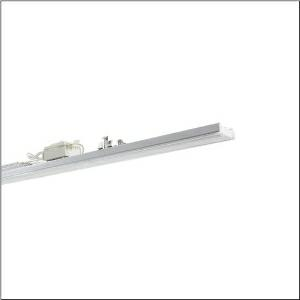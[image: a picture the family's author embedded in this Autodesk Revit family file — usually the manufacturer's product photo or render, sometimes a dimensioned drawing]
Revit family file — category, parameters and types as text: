
# Revit family: licross_11_recessed_mo_51tl18vn455g
name_source: partatom
category: Lighting Fixtures
units: mm (PartAtom-declared; Revit-internal decimal feet)

## family parameters
Cut with Voids When Loaded = No
Host = Face
Light Source = No
Part Type = Normal
Room Calculation Point = No
Round Connector Dimension = Use Diameter
Shared = No

## types (1)
- --- (1 x LED, 5560 lm, 30 W, 4000K)
    Apparent Load = 30 VA
    CIE Flux Codes = 83 96 99 100 100
    Color Rendering = 80
    Color Temperature = 4000K
    Default Elevation = 1800 mm
    Description = Licross 11 Recessed MO, luminaire insert, of sheet steel, galvanised, coil coated, white, length: 1.500mm, width: 66mm, height: 67mm, LED rated luminous flux: 5.560lm, light colour: 840, SDCM (Standard Deviation of Colour Matching)MacAdam ≤ 2 SDCM (initial), control gear: DALI 2, CLO, with plug, 5-pole, with phase selection, mains connection: 220..240V, AC, 50/60Hz, start of lifetime: 30W, end of service life: 34W, internal wiring halogen-free, primary optical cover: cover, of PMMA, light emission: direct distribution, primary light characteristic: symmetric, protection rating (complete): IP40, insulation class (complete): insulation class I (protective earthing), certification: CE, ENEC, VDE, UKCA, protection symbol: D if used in an environment without relevant dust loads with corresponding accessories, impact resistance: IK06, permissible ambient temperature for indoor applications: -25..+40°C, corresponds to IFS (International Featured Standards) requirements for safety and quality in the food industry, reducing of maximum allowable ambient temperature of 5°C with ceiling mounting, LABS conformity tested according to VDMA 24364:2018-05, The light source and the operating device comply with the requirements of the Ecodesign Regulation (EU) 2019/2020 and are replaceable in accordance with this regulation, packaging unit: 1 piece
    Height = 58 mm
    Lamp = 1 x LED
    Lamp Light Flux = 5560 lm
    Lamp Power = 30 W
    Lamp count = 1
    Length = 1500 mm
    Luminous efficacy = 185 lm/W
    Manufacturer = Siteco
    ModVariant = No
    Model = 51TL18VN455G
    Mounting Place = Ceiling
    Mounting Type = Pendant
    Number of Poles = 1
    OnlyDefault = Yes
    Power Factor = 1
    Product Name = Licross 11 Recessed MO
    Product group = luminaire insert | ceiling pendant
    ProductGroupID = 901
    Protection Class = Protection class I
    Protection Degree = IP 40
    RLX_Detail_Level = 1
    RLX_Emergency_Light_Flux = 0 lm
    RLX_Emergency_Type = 0
    RLX_Emergency_Type_DB = No
    RlxData = <blob elided: 24409 chars, md5=9c7b2421>
    Socket = socket
    Standby Power = 0 W
    System Light Flux = 5560 lm
    System Power = 30 W
    Type Comments = factory setting: luminous flux: 100 % | dim-lin: 254 | 203 mA
    Type Image = l_1296930.jpg
    URL = http://relux.com
    VarID = @adj_055991
    Voltage = 0 V
    Weight = 0.00 kg
    Width = 66 mm

## geometry (parser evidence)
native form markers: Blend x4, Sweep x10
no freeform markers — native parametric forms only
